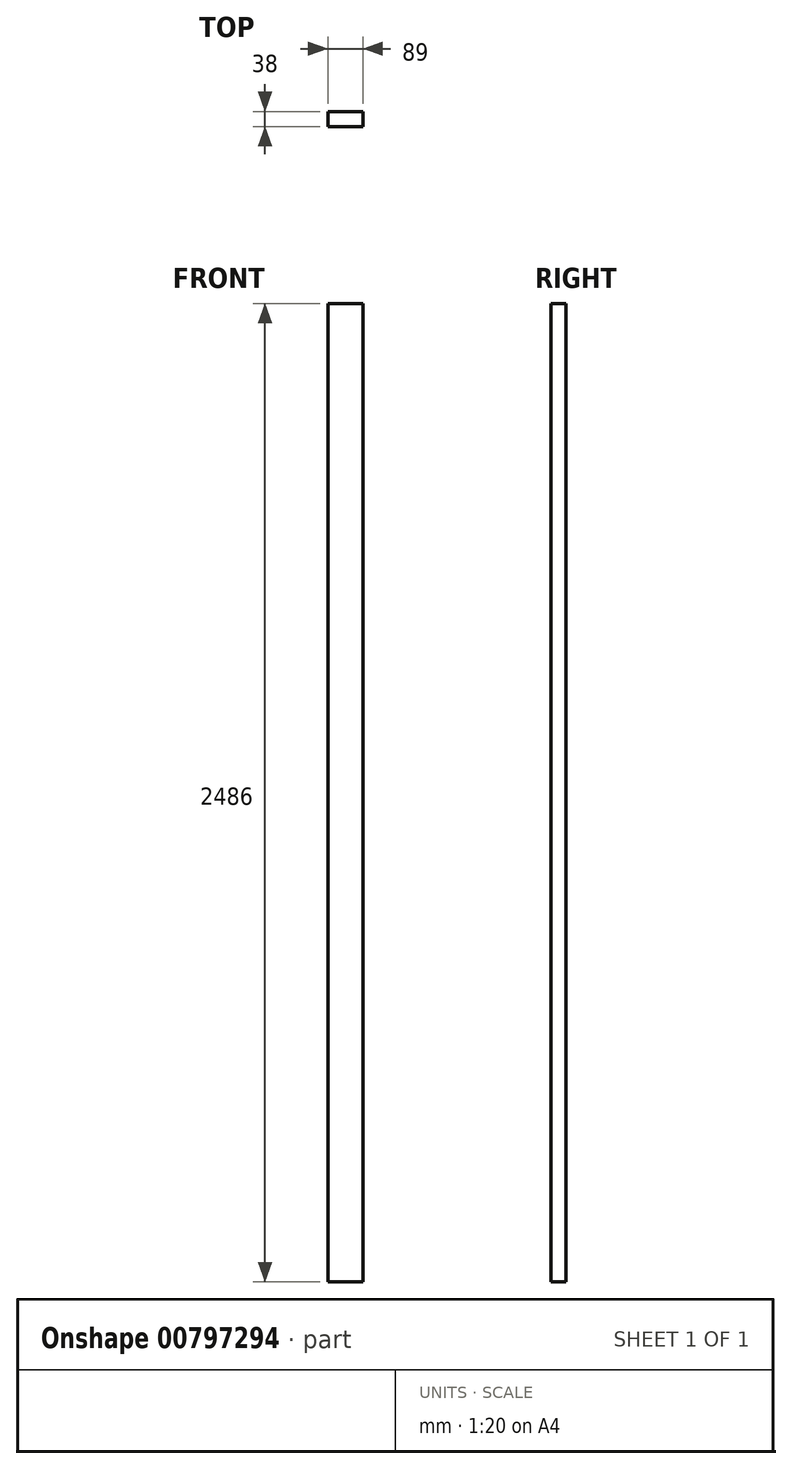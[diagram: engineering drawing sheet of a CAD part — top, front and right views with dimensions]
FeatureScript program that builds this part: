
annotation { "Feature Type Name" : "Feature", "Feature Type Description" : "" }
export const myFeature = defineFeature(function(context is Context, id is Id, definition is map)
    precondition{}
    {
        {
            var Q0;
            Q0=qCreatedBy(makeId("Top.planeOp"),FACE);
            var sketch = newSketch(context, id + "F0", { "sketchPlane" : qUnion([Q0])});
            skLineSegment(sketch, "E0.bottom", {"start": v(44.5, 19) * mm, "end": v(-44.5, 19) * mm});
            skLineSegment(sketch, "E0.top", {"start": v(44.5, -19) * mm, "end": v(-44.5, -19) * mm});
            skLineSegment(sketch, "E0.left", {"start": v(44.5, 19) * mm, "end": v(44.5, -19) * mm});
            skLineSegment(sketch, "E0.right", {"start": v(-44.5, 19) * mm, "end": v(-44.5, -19) * mm});
            skPoint(sketch, "E0.middle", {"position": v(0, 0) * mm});
            skSolve(sketch);
        }
        {
            var Q0;
            Q0 = qSketchRegion(id + "F0", true);
            extrude(context, id + "F1", {"entities" : qUnion([Q0]), "depth" : 2486 * mm, "offsetDistance" : 25 * mm, "symmetric" : true});
        }
    });
